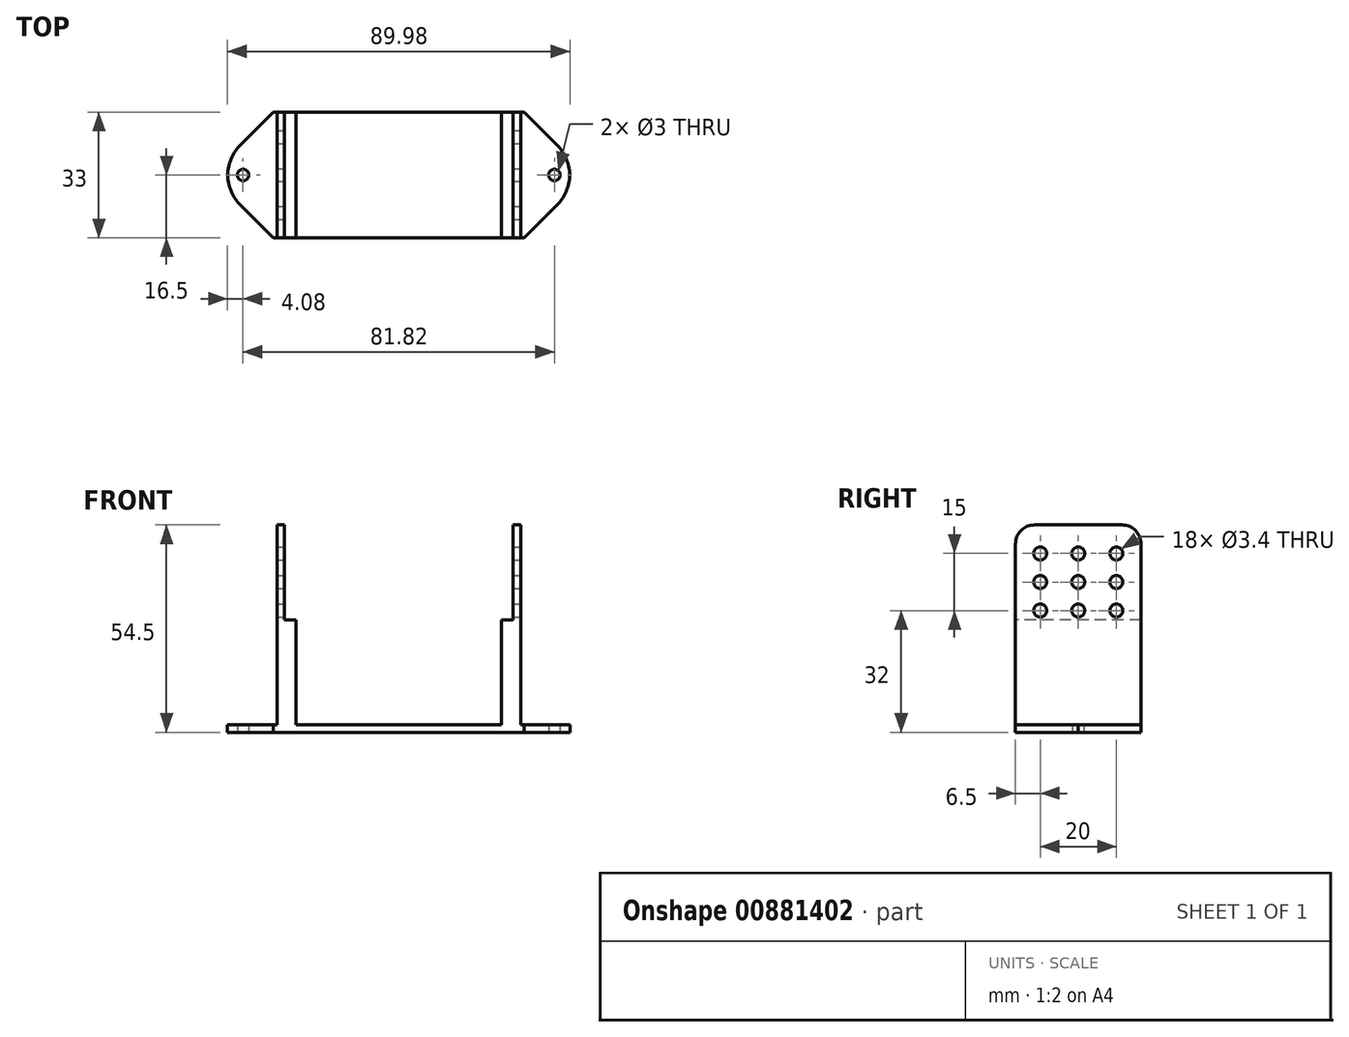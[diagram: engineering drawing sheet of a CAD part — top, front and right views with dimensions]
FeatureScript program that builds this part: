
annotation { "Feature Type Name" : "Feature", "Feature Type Description" : "" }
export const myFeature = defineFeature(function(context is Context, id is Id, definition is map)
    precondition{}
    {
        {
            var Q0;
            Q0=qCreatedBy(makeId("Top.planeOp"),FACE);
            var sketch = newSketch(context, id + "F0", { "sketchPlane" : qUnion([Q0])});
            skLineSegment(sketch, "E0.bottom", {"start": v(45, -16.5) * mm, "end": v(-45, -16.5) * mm});
            skLineSegment(sketch, "E0.top", {"start": v(45, 16.5) * mm, "end": v(-45, 16.5) * mm});
            skLineSegment(sketch, "E0.left", {"start": v(45, -16.5) * mm, "end": v(45, 16.5) * mm});
            skLineSegment(sketch, "E0.right", {"start": v(-45, -16.5) * mm, "end": v(-45, 16.5) * mm});
            skPoint(sketch, "E0.middle", {"position": v(0, 0) * mm});
            skPoint(sketch, "E1", {"position": v(-40.9, 0) * mm});
            skPoint(sketch, "E2", {"position": v(40.9, 0) * mm});
            skPoint(sketch, "E2.positionSnap0", {"position": v(45, 0) * mm});
            skCircle(sketch, "E3", {"center": v(-40.9, 0) * mm, "radius": 1.5 * mm});
            skCircle(sketch, "E4", {"center": v(40.9, 0) * mm, "radius": 1.5 * mm});
            skSolve(sketch);
        }
        {
            var Q0;
            Q0=makeQuery(id+"F0.imprint","IMPRINT",FACE,{"disambiguationData":[TD([[makeQuery(id+"F0.imprint","IMPRINT",EDGE,{"derivedFrom":sQuery(id+"F0.wireOp",EDGE,"E0.bottom")}),-1.0]])]});
            extrude(context, id + "F1", {"entities" : qUnion([Q0]), "depth" : 2 * mm, "offsetDistance" : 25 * mm});
        }
        {
            var Q0;
            Q0=makeQuery(id+"F1.opExtrude","CAP_FACE",FACE,{"disambiguationData":[OSD([sQuery(id+"F0.wireOp",EDGE,"E0.bottom"),sQuery(id+"F0.wireOp",EDGE,"E0.top"),sQuery(id+"F0.wireOp",EDGE,"E0.left"),sQuery(id+"F0.wireOp",EDGE,"E0.right"),sQuery(id+"F0.wireOp",EDGE,"E3"),sQuery(id+"F0.wireOp",EDGE,"E4")])],"isStart":false});
            var sketch = newSketch(context, id + "F2", { "sketchPlane" : qUnion([Q0])});
            skPoint(sketch, "E5", {"position": v(-32, 16.5) * mm});
            skPoint(sketch, "E6", {"position": v(-32, -16.5) * mm});
            skPoint(sketch, "E7", {"position": v(32, 16.5) * mm});
            skPoint(sketch, "E8", {"position": v(32, -16.5) * mm});
            skPoint(sketch, "E9", {"position": v(-27, 16.5) * mm});
            skPoint(sketch, "E10", {"position": v(-27, -16.5) * mm});
            skPoint(sketch, "E11", {"position": v(27, 16.5) * mm});
            skLineSegment(sketch, "E12", {"start": v(-32, 16.5) * mm, "end": v(-32, -16.5) * mm});
            skLineSegment(sketch, "E13", {"start": v(-27, -16.5) * mm, "end": v(-27, 16.5) * mm});
            skLineSegment(sketch, "E14", {"start": v(32, -16.5) * mm, "end": v(32, 16.5) * mm});
            skPoint(sketch, "E15", {"position": v(27, -16.5) * mm});
            skLineSegment(sketch, "E16", {"start": v(27, 16.5) * mm, "end": v(27, -16.5) * mm});
            skSolve(sketch);
        }
        {
            var Q0;
            {var subQ0=sQuery(id+"F2.wireOp",EDGE,"E12");Q0=makeQuery(id+"F2.imprint","IMPRINT",FACE,{"disambiguationData":[TD([[makeQuery(id+"F2.imprint","IMPRINT",EDGE,{"derivedFrom":subQ0}),1.0]])]});}
            var Q1;
            {var subQ0=sQuery(id+"F2.wireOp",EDGE,"E14");Q1=makeQuery(id+"F2.imprint","IMPRINT",FACE,{"disambiguationData":[TD([[makeQuery(id+"F2.imprint","IMPRINT",EDGE,{"derivedFrom":subQ0}),1.0]])]});}
            extrude(context, id + "F3", {"entities" : qUnion([Q0, Q1]), "operationType" : NewBodyOperationType.ADD, "depth" : 27.5 * mm, "offsetDistance" : 25 * mm});
        }
        {
            var Q0;
            Q0=makeQuery(id+"F3.opExtrude","CAP_FACE",FACE,{"disambiguationData":[OSD([sQuery(id+"F0.wireOp",EDGE,"E0.bottom"),sQuery(id+"F0.wireOp",EDGE,"E0.top"),sQuery(id+"F2.wireOp",EDGE,"E12"),sQuery(id+"F2.wireOp",EDGE,"E13")])],"isStart":false});
            var sketch = newSketch(context, id + "F4", { "sketchPlane" : qUnion([Q0])});
            skPoint(sketch, "E17", {"position": v(-30, 0) * mm});
            skPoint(sketch, "E17.positionSnap0", {"position": v(-27, 0) * mm});
            skPoint(sketch, "E18", {"position": v(-30, 16.5) * mm});
            skPoint(sketch, "E19", {"position": v(-30, -16.5) * mm});
            skLineSegment(sketch, "E20", {"start": v(-30, 16.5) * mm, "end": v(-30, -16.5) * mm});
            skSolve(sketch);
        }
        {
            var Q0;
            {var subQ0=sQuery(id+"F4.wireOp",EDGE,"E20");Q0=makeQuery(id+"F4.imprint","IMPRINT",FACE,{"disambiguationData":[TD([[makeQuery(id+"F4.imprint","IMPRINT",EDGE,{"derivedFrom":subQ0}),-1.0]])]});}
            extrude(context, id + "F5", {"entities" : qUnion([Q0]), "operationType" : NewBodyOperationType.ADD, "depth" : 25 * mm, "offsetDistance" : 25 * mm});
        }
        {
            var Q0;
            Q0=makeQuery(id+"F3.opExtrude","CAP_FACE",FACE,{"disambiguationData":[OSD([sQuery(id+"F0.wireOp",EDGE,"E0.bottom"),sQuery(id+"F0.wireOp",EDGE,"E0.top"),sQuery(id+"F2.wireOp",EDGE,"E14"),sQuery(id+"F2.wireOp",EDGE,"E16")])],"isStart":false});
            var sketch = newSketch(context, id + "F6", { "sketchPlane" : qUnion([Q0])});
            skPoint(sketch, "E21", {"position": v(30, 0) * mm});
            skPoint(sketch, "E21.positionSnap0", {"position": v(32, 0) * mm});
            skPoint(sketch, "E22", {"position": v(30, 16.5) * mm});
            skPoint(sketch, "E23", {"position": v(30, -16.5) * mm});
            skLineSegment(sketch, "E24", {"start": v(30, 16.5) * mm, "end": v(30, -16.5) * mm});
            skSolve(sketch);
        }
        {
            var Q0;
            {var subQ0=sQuery(id+"F6.wireOp",EDGE,"E24");Q0=makeQuery(id+"F6.imprint","IMPRINT",FACE,{"disambiguationData":[TD([[makeQuery(id+"F6.imprint","IMPRINT",EDGE,{"derivedFrom":subQ0}),1.0]])]});}
            extrude(context, id + "F7", {"entities" : qUnion([Q0]), "operationType" : NewBodyOperationType.ADD, "depth" : 25 * mm, "offsetDistance" : 25 * mm});
        }
        {
            var Q0;
            {var subQ0=sQuery(id+"F2.wireOp",EDGE,"E12");Q0=makeQuery(id+"F5.boolean.opBoolean","MERGE",FACE,{"derivedFrom":[makeQuery(id+"F3.opExtrude","SWEPT_FACE",FACE,{"disambiguationData":[OSD([subQ0])]}),makeQuery(id+"F5.opExtrude","SWEPT_FACE",FACE,{"disambiguationData":[OSD([subQ0])]})]});}
            var sketch = newSketch(context, id + "F8", { "sketchPlane" : qUnion([Q0])});
            skPoint(sketch, "E25", {"position": v(0, 39.5) * mm});
            skPoint(sketch, "E25.positionSnap0", {"position": v(0, 54.5) * mm});
            skPoint(sketch, "E26", {"position": v(10, 39.5) * mm});
            skPoint(sketch, "E27", {"position": v(-10, 39.5) * mm});
            skPoint(sketch, "E28", {"position": v(-10, 47) * mm});
            skPoint(sketch, "E29", {"position": v(0, 47) * mm});
            skPoint(sketch, "E30", {"position": v(10, 47) * mm});
            skPoint(sketch, "E31", {"position": v(-10, 32) * mm});
            skPoint(sketch, "E32", {"position": v(0, 32) * mm});
            skPoint(sketch, "E33", {"position": v(10, 32) * mm});
            skSolve(sketch);
        }
        {
            var Q0;
            Q0=sQuery(id+"F8.wireOp",VERTEX,"E28");
            var Q1;
            Q1=sQuery(id+"F8.wireOp",VERTEX,"E27");
            var Q2;
            Q2=sQuery(id+"F8.wireOp",VERTEX,"E25");
            var Q3;
            Q3=sQuery(id+"F8.wireOp",VERTEX,"E29");
            var Q4;
            Q4=sQuery(id+"F8.wireOp",VERTEX,"E30");
            var Q5;
            Q5=sQuery(id+"F8.wireOp",VERTEX,"E26");
            var Q6;
            Q6=sQuery(id+"F8.wireOp",VERTEX,"E31");
            var Q7;
            Q7=sQuery(id+"F8.wireOp",VERTEX,"E32");
            var Q8;
            Q8=sQuery(id+"F8.wireOp",VERTEX,"E33");
            var Q9;
            Q9=makeQuery(id+"F1.opExtrude","SWEPT_BODY",BODY,{"disambiguationData":[OSD([sQuery(id+"F0.wireOp",EDGE,"E0.bottom"),sQuery(id+"F0.wireOp",EDGE,"E0.top"),sQuery(id+"F0.wireOp",EDGE,"E0.left"),sQuery(id+"F0.wireOp",EDGE,"E0.right"),sQuery(id+"F0.wireOp",EDGE,"E3"),sQuery(id+"F0.wireOp",EDGE,"E4")])]});
            hole(context, id + "F9", {"style" : HoleStyle.SIMPLE, "endStyle" : HoleEndStyle.THROUGH, "standardTappedOrClearance" : lookupTablePath({ "fit" : "Normal", "standard" : "ISO", "size" : "M3", "type" : "Clearance" }), "standardBlindInLast" : lookupTablePath({ "fit" : "Normal", "standard" : "ISO", "engagement" : "75%", "pitch" : "0.5 mm", "size" : "M3", "type" : "Clearance & tapped" }), "holeDiameter" : 3.4 * mm, "majorDiameter" : 5 * mm, "isTappedThrough" : true, "tappedDepth" : 12 * mm, "tapClearance" : 3, "locations" : qUnion([Q0, Q1, Q2, Q3, Q4, Q5, Q6, Q7, Q8]), "scope" : qUnion([Q9]), "startStyle" : HoleStartStyle.SKETCH});
        }
        {
            var Q0;
            Q0=makeQuery(id+"F5.opExtrude","CAP_EDGE",EDGE,{"disambiguationData":[OSD([sQuery(id+"F0.wireOp",EDGE,"E0.top")])],"isStart":false});
            var Q1;
            Q1=makeQuery(id+"F5.opExtrude","CAP_EDGE",EDGE,{"disambiguationData":[OSD([sQuery(id+"F0.wireOp",EDGE,"E0.bottom")])],"isStart":false});
            var Q2;
            Q2=makeQuery(id+"F7.opExtrude","CAP_EDGE",EDGE,{"disambiguationData":[OSD([sQuery(id+"F0.wireOp",EDGE,"E0.top")])],"isStart":false});
            var Q3;
            Q3=makeQuery(id+"F7.opExtrude","CAP_EDGE",EDGE,{"disambiguationData":[OSD([sQuery(id+"F0.wireOp",EDGE,"E0.bottom")])],"isStart":false});
            fillet(context, id + "F10", {"entities" : qUnion([Q0, Q1, Q2, Q3]), "tangentPropagation" : true, "radius" : 5 * mm, "defaultsChanged" : false, "vertexSettings" : [], "allowEdgeOverflow" : false});
        }
        {
            var Q0;
            Q0=makeQuery(id+"F1.opExtrude","SWEPT_EDGE",EDGE,{"disambiguationData":[OSD([sQuery(id+"F0.wireOp",EDGE,"E0.top"),sQuery(id+"F0.wireOp",EDGE,"E0.left")])]});
            var Q1;
            Q1=makeQuery(id+"F1.opExtrude","SWEPT_EDGE",EDGE,{"disambiguationData":[OSD([sQuery(id+"F0.wireOp",EDGE,"E0.bottom"),sQuery(id+"F0.wireOp",EDGE,"E0.left")])]});
            var Q2;
            Q2=makeQuery(id+"F1.opExtrude","SWEPT_EDGE",EDGE,{"disambiguationData":[OSD([sQuery(id+"F0.wireOp",EDGE,"E0.bottom"),sQuery(id+"F0.wireOp",EDGE,"E0.right")])]});
            var Q3;
            Q3=makeQuery(id+"F1.opExtrude","SWEPT_EDGE",EDGE,{"disambiguationData":[OSD([sQuery(id+"F0.wireOp",EDGE,"E0.top"),sQuery(id+"F0.wireOp",EDGE,"E0.right")])]});
            chamfer(context, id + "F11", {"entities" : qUnion([Q0, Q1, Q2, Q3]), "width" : 12 * mm, "tangentPropagation" : true});
        }
        {
            var Q0;
            {var subQ0=sQuery(id+"F0.wireOp",EDGE,"E0.left");Q0=makeQuery(id+"F11.opChamfer","BLEND_EDGE",EDGE,{"blendedFrom":[makeQuery(id+"F1.opExtrude","SWEPT_EDGE",EDGE,{"disambiguationData":[OSD([sQuery(id+"F0.wireOp",EDGE,"E0.bottom"),subQ0])]}),makeQuery(id+"F1.opExtrude","SWEPT_FACE",FACE,{"disambiguationData":[OSD([subQ0])]})],"blendedInto":[makeQuery(id+"F1.opExtrude","SWEPT_FACE",FACE,{"disambiguationData":[OSD([subQ0])]})]});}
            var Q1;
            {var subQ0=sQuery(id+"F0.wireOp",EDGE,"E0.left");Q1=makeQuery(id+"F11.opChamfer","BLEND_EDGE",EDGE,{"blendedFrom":[makeQuery(id+"F1.opExtrude","SWEPT_EDGE",EDGE,{"disambiguationData":[OSD([sQuery(id+"F0.wireOp",EDGE,"E0.top"),subQ0])]}),makeQuery(id+"F1.opExtrude","SWEPT_FACE",FACE,{"disambiguationData":[OSD([subQ0])]})],"blendedInto":[makeQuery(id+"F1.opExtrude","SWEPT_FACE",FACE,{"disambiguationData":[OSD([subQ0])]})]});}
            var Q2;
            {var subQ0=sQuery(id+"F0.wireOp",EDGE,"E0.right");Q2=makeQuery(id+"F11.opChamfer","BLEND_EDGE",EDGE,{"blendedFrom":[makeQuery(id+"F1.opExtrude","SWEPT_EDGE",EDGE,{"disambiguationData":[OSD([sQuery(id+"F0.wireOp",EDGE,"E0.bottom"),subQ0])]}),makeQuery(id+"F1.opExtrude","SWEPT_FACE",FACE,{"disambiguationData":[OSD([subQ0])]})],"blendedInto":[makeQuery(id+"F1.opExtrude","SWEPT_FACE",FACE,{"disambiguationData":[OSD([subQ0])]})]});}
            var Q3;
            {var subQ0=sQuery(id+"F0.wireOp",EDGE,"E0.right");Q3=makeQuery(id+"F11.opChamfer","BLEND_EDGE",EDGE,{"blendedFrom":[makeQuery(id+"F1.opExtrude","SWEPT_EDGE",EDGE,{"disambiguationData":[OSD([sQuery(id+"F0.wireOp",EDGE,"E0.top"),subQ0])]}),makeQuery(id+"F1.opExtrude","SWEPT_FACE",FACE,{"disambiguationData":[OSD([subQ0])]})],"blendedInto":[makeQuery(id+"F1.opExtrude","SWEPT_FACE",FACE,{"disambiguationData":[OSD([subQ0])]})]});}
            fillet(context, id + "F12", {"entities" : qUnion([Q0, Q1, Q2, Q3]), "tangentPropagation" : true, "radius" : 12.14 * mm, "defaultsChanged" : false, "vertexSettings" : [], "allowEdgeOverflow" : false});
        }
    });
